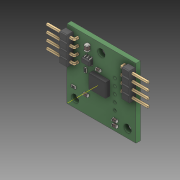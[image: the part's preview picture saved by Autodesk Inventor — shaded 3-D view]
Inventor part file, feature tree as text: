
AUTODESK INVENTOR PART (.ipt)
format: ipt  version: 2020 (Build 240168000, 168)  size: 615,424 bytes
history: native  units: in
note: dims shown in document units (in); Inventor stores cm internally (conversion verified against a paired STEP export)
features: other x13, sketch x1
ambient origin geometry x8: Origin, YZ Plane, XZ Plane, XY Plane, X Axis, Y Axis, Z Axis, Center Point
bodies: Solid1 (feature_tree)
feature tree (14):
  other  "SmallEncoder.iam"
  other  "C_0603_1608Metric.iam:1::SOLID_1.ipt:1"
  other  "C_0603_1608Metric.iam:2::SOLID_1.ipt:1"
  other  "C_0603_1608Metric.iam:3::SOLID_1.ipt:1"
  other  "R_0603_1608Metric.iam:1::SOLID_2.ipt:1"
  other  "R_0603_1608Metric.iam:2::SOLID_2.ipt:1"
  other  "C_0603_1608Metric.iam:4::SOLID_1.ipt:1"
  other  "C_0805_2012Metric.iam:1::SOLID_3.ipt:1"
  other  "PinHeader_1x04_P2.54mm_Horizontal.iam:1::SOLID_4.ipt:1"
  other  "PinHeader_1x04_P2.54mm_Horizontal.iam:2::SOLID_4.ipt:1"
  other  "SOT-23-5.iam:1::SOLID_5.ipt:1"
  other  "COMPOUND.ipt:1"
  sketch  "Sketch1"  dims[d0=0.3937in]
  other  "Work Axis1"
